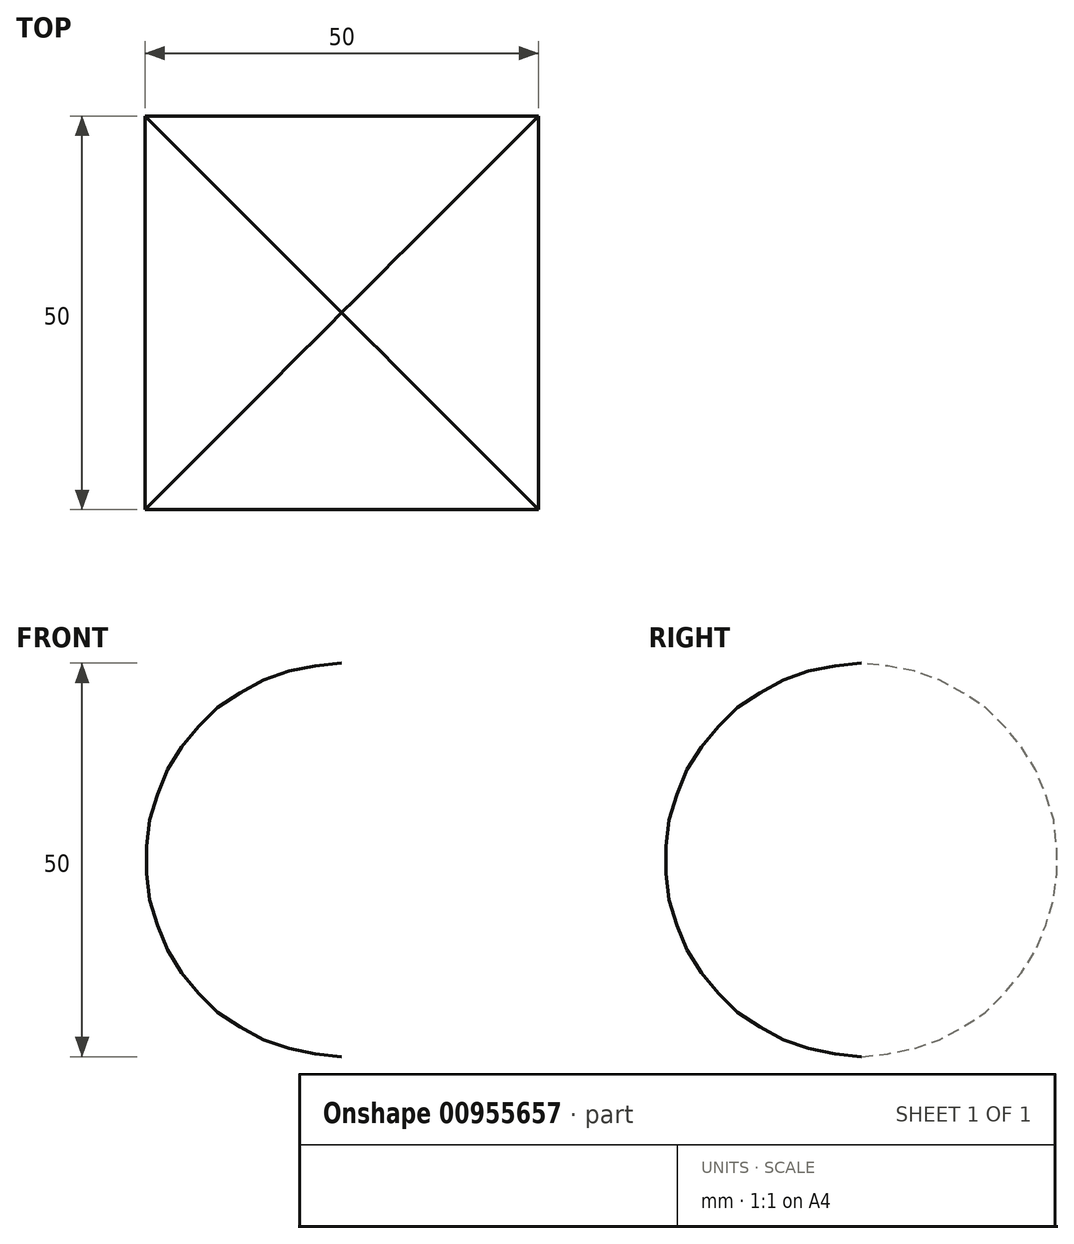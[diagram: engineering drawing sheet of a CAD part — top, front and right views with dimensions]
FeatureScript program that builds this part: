
annotation { "Feature Type Name" : "Feature", "Feature Type Description" : "" }
export const myFeature = defineFeature(function(context is Context, id is Id, definition is map)
    precondition{}
    {
        {
            var Q0;
            Q0=qCreatedBy(makeId("Front.planeOp"),FACE);
            var sketch = newSketch(context, id + "F0", { "sketchPlane" : qUnion([Q0])});
            skCircle(sketch, "E0", {"center": v(0, 0) * mm, "radius": 25 * mm});
            skSolve(sketch);
        }
        {
            var Q0;
            Q0 = qSketchRegion(id + "F0", true);
            extrude(context, id + "F1", {"entities" : qUnion([Q0]), "endBound" : BoundingType.SYMMETRIC, "depth" : 100 * mm, "offsetDistance" : 25 * mm});
        }
        {
            var Q0;
            Q0=qCreatedBy(makeId("Right.planeOp"),FACE);
            var sketch = newSketch(context, id + "F2", { "sketchPlane" : qUnion([Q0])});
            skCircle(sketch, "E1", {"center": v(0, 0) * mm, "radius": 25 * mm});
            skLineSegment(sketch, "E2.bottom", {"start": v(75, 75) * mm, "end": v(-75, 75) * mm});
            skLineSegment(sketch, "E2.top", {"start": v(75, -75) * mm, "end": v(-75, -75) * mm});
            skLineSegment(sketch, "E2.left", {"start": v(75, 75) * mm, "end": v(75, -75) * mm});
            skLineSegment(sketch, "E2.right", {"start": v(-75, 75) * mm, "end": v(-75, -75) * mm});
            skSolve(sketch);
        }
        {
            var Q0;
            Q0=makeQuery(id+"F2.imprint","IMPRINT",FACE,{"disambiguationData":[TD([[makeQuery(id+"F2.imprint","IMPRINT",EDGE,{"derivedFrom":sQuery(id+"F2.wireOp",EDGE,"E1")}),-1.0]])]});
            extrude(context, id + "F3", {"entities" : qUnion([Q0]), "operationType" : NewBodyOperationType.REMOVE, "endBound" : BoundingType.SYMMETRIC, "oppositeDirection" : true, "depth" : 100 * mm, "offsetDistance" : 25 * mm});
        }
    });
